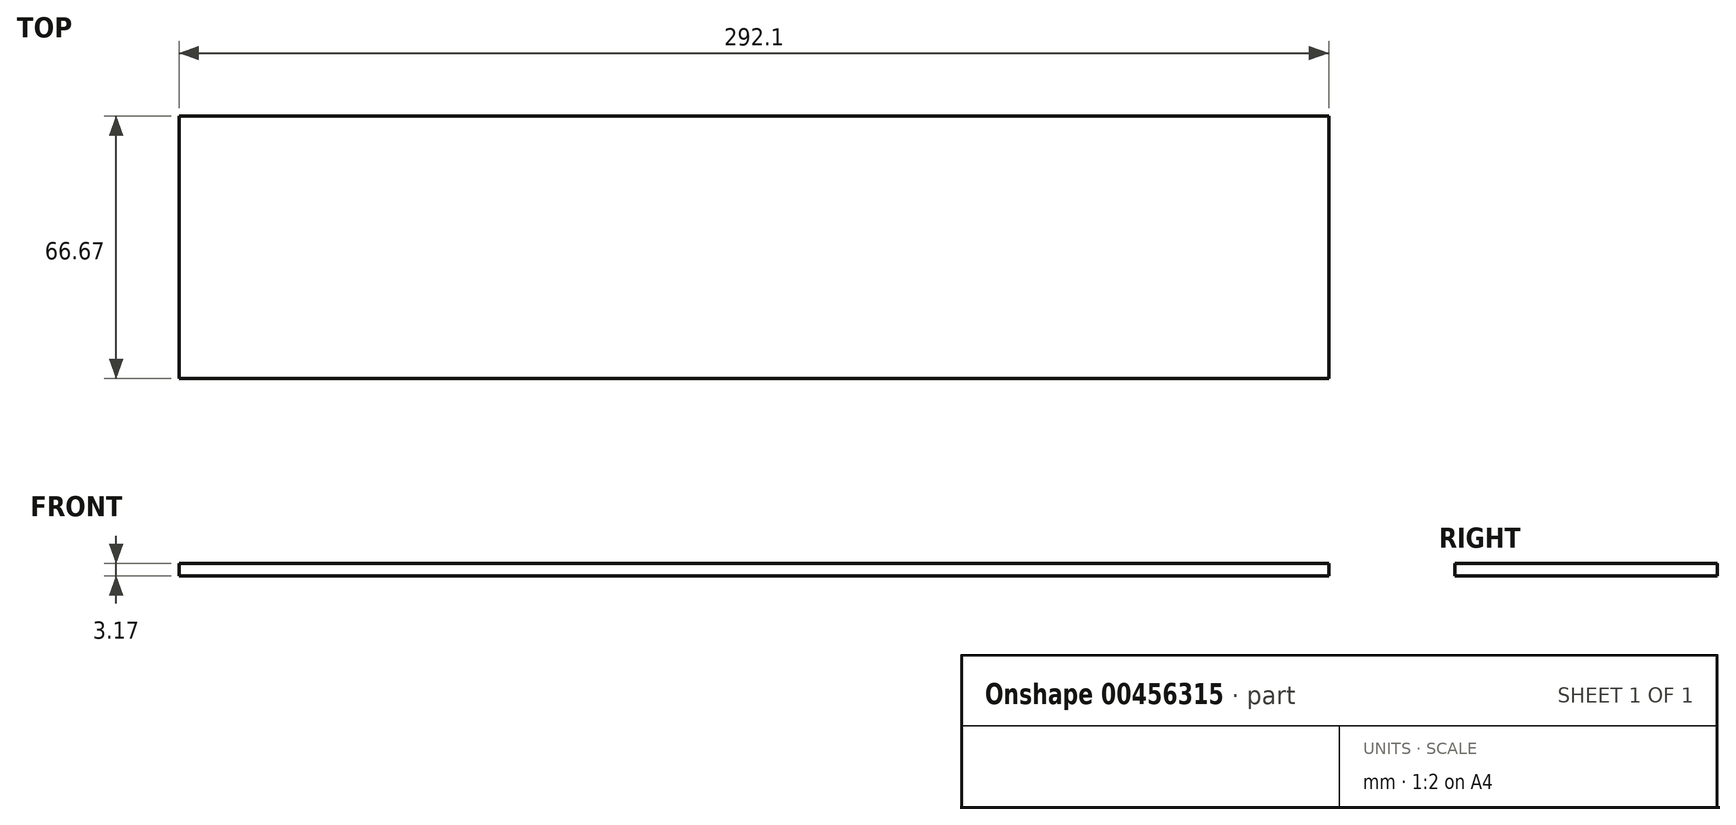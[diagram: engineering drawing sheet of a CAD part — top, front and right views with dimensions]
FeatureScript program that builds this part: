
annotation { "Feature Type Name" : "Feature", "Feature Type Description" : "" }
export const myFeature = defineFeature(function(context is Context, id is Id, definition is map)
    precondition{}
    {
        {
            var Q0;
            Q0=qCreatedBy(makeId("Top.planeOp"),FACE);
            var sketch = newSketch(context, id + "F0", { "sketchPlane" : qUnion([Q0])});
            skLineSegment(sketch, "E0.bottom", {"start": v(0, 0) * mm, "end": v(292.1, 0) * mm});
            skLineSegment(sketch, "E0.top", {"start": v(0, 66.68) * mm, "end": v(292.1, 66.68) * mm});
            skLineSegment(sketch, "E0.left", {"start": v(0, 0) * mm, "end": v(0, 66.68) * mm});
            skLineSegment(sketch, "E0.right", {"start": v(292.1, 0) * mm, "end": v(292.1, 66.68) * mm});
            skSolve(sketch);
        }
        {
            var Q0;
            Q0=makeQuery(id+"F0.imprint","IMPRINT",FACE,{"disambiguationData":[TD([[makeQuery(id+"F0.imprint","IMPRINT",EDGE,{"derivedFrom":sQuery(id+"F0.wireOp",EDGE,"E0.bottom")}),1.0]])]});
            extrude(context, id + "F1", {"entities" : qUnion([Q0]), "depth" : 3.17 * mm});
        }
    });
